# Revit family: 5LBS6030B17T,B2T,B17B,B2B
name_source: partatom
category: Plumbing Fixtures
revit_build: Autodesk Revit LT 2014 (Build: 20130308_1515(x64)
units: mm (PartAtom-declared; Revit-internal decimal feet)

## types (4) — shared parameters
Assembly Code = D2010710
Keynote = 22 40 00.B3
Manufacturer = Best Bath Systems, Inc.
Type Comments = Barrier Free
URL = http://www.best-bath.com
Unit Width = 60"

## per-type parameters (varying)
| type | Description | Threshold Height | Unit Height |
| 5LBS6030B17B | 4 x8 Subway Tile, Beveled Threshold | 1 3/4" | 82 1/4" |
| 5LBS6030B17T | 4 x 8 SubwayTile, Traditionals Bull Nose Threshold | 1 3/4" | 82 1/4" |
| 5LBS6030B2T | 4 x 8 Subway Tile, Traditionals Bull Nose Threshold | 2" | 82 1/2" |
| 5LBS6030B2B | 4 x 8 Subway Tile, Beveled Threshold | 2" | 82 1/2" |

note: column(s) folded — value = type name in every type: Model

## geometry (parser evidence)
native form markers: Blend x16, Sweep x1
no freeform markers — native parametric forms only
